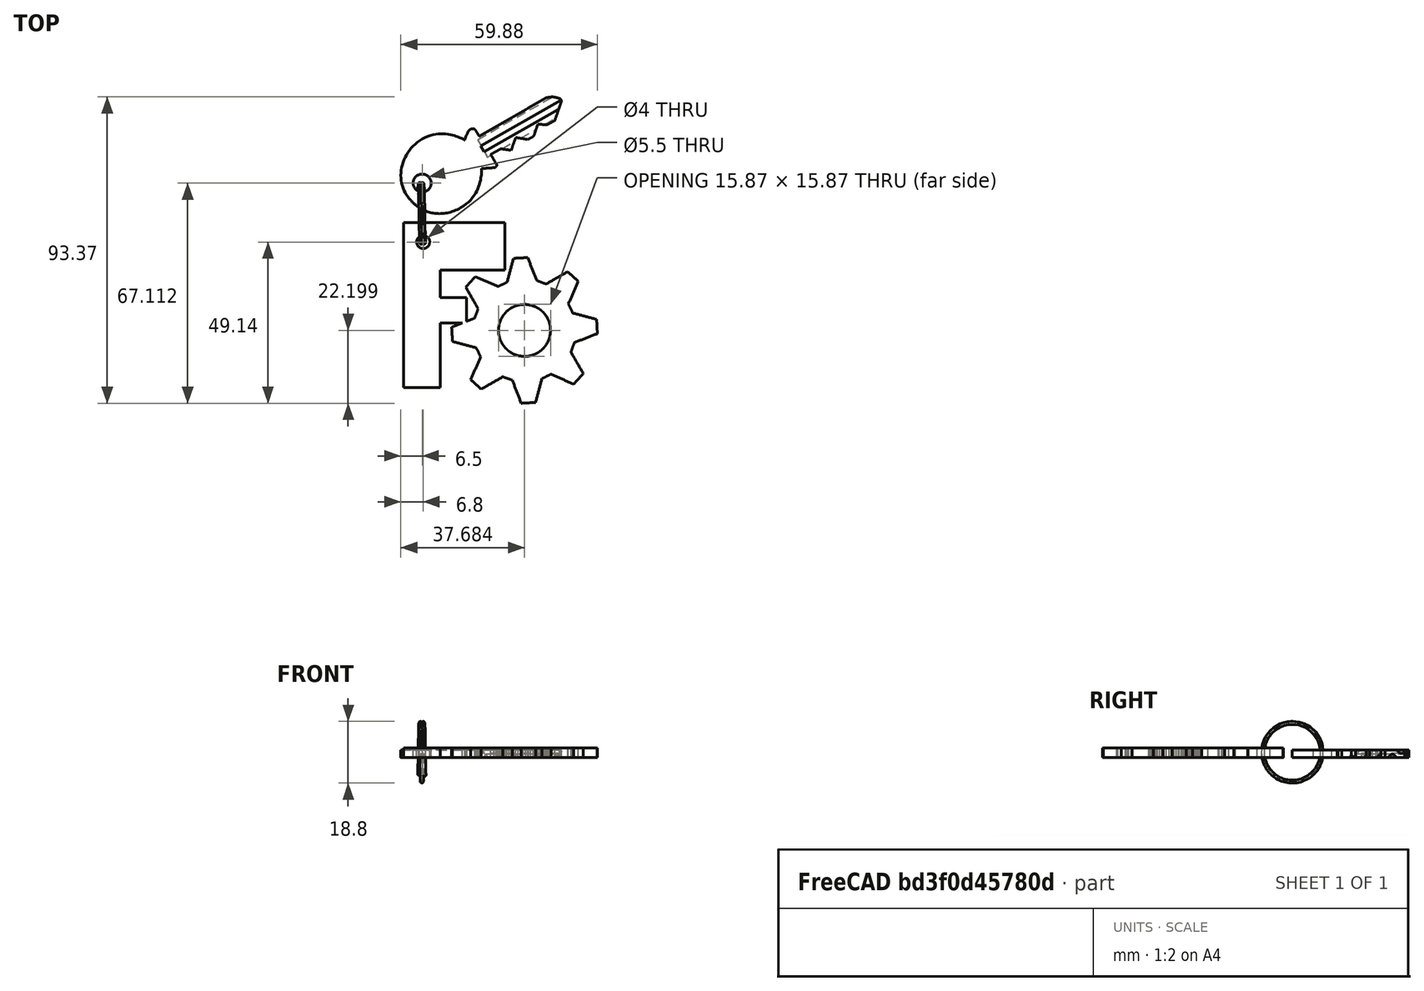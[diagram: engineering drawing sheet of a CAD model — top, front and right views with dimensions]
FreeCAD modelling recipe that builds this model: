
FCSTD DOCUMENT  (FreeCAD 0.15R4630 (Git))
Label: freecad
License: CreativeCommons Attribution-ShareAlike
LicenseURL: http://creativecommons.org/licenses/by-sa/4.0/
objects: Part::Feature×5, Part::Extrusion×3, App::DocumentObjectGroup×2, Part::Cut×2, Part::MultiFuse×1, Part::Cylinder×1
note: 12 computed .brp shape members not serialized (recipe doc carries the construction recipe); baked Part::Feature solids carry a one-line shape summary decoded from their .brp

FEATURE [Part::Feature] Sweep  label="key-ring-model-1"
  Placement = pos=(-1.2,24.7546,1.6391) rot=(0.333333,0.881918,0.333333;1.69612rad)
  shape: bbox 3.31 x 27.02 x 26.33 mm, 4 faces (baked)
FEATURE [Part::Feature] Cut  label="key-model-1"
  Placement = pos=(-5.46976,31.0266,0) rot=(0,0,1;0.517888rad)
  shape: bbox 49.82 x 36.6 x 2.3 mm, 44 faces (baked)
FEATURE [App::DocumentObjectGroup] Group  label="Assembly"
  Group = -> [Sweep,Cut]
FEATURE [Part::Feature] rect3663
  shape: bbox 30.8 x 50.38 x 7.562e-07 mm, 0 faces, 0 solids (baked)
FEATURE [Part::Feature] path3659
  shape: bbox 44.4 x 44.4 x 7.562e-07 mm, 0 faces, 0 solids (baked)
FEATURE [Part::Feature] path3659001
  shape: bbox 15.87 x 15.87 x 7.562e-07 mm, 0 faces, 0 solids (baked)
FEATURE [Part::Extrusion] Extrude
  Base = -> rect3663
  Dir = (0,0,3)
  Solid = true
FEATURE [Part::Extrusion] Extrude001
  Base = -> path3659
  Dir = (0,0,3)
  Solid = true
FEATURE [Part::Extrusion] Extrude002
  Base = -> path3659001
  Dir = (0,0,3)
  Solid = true
FEATURE [Part::Cut] Cut001
  Base = -> Extrude001
  Tool = -> Extrude002
FEATURE [Part::MultiFuse] Fusion  label="Logo"
  Shapes = -> [Extrude,Cut001]
FEATURE [Part::Cylinder] Cylinder  label="drill"
  Angle = 360
  Height = 10
  Placement = pos=(7,-7,0) rot=(0,0,1;0rad)
  Radius = 2
FEATURE [Part::Cut] Cut002  label="freecad-key"
  Base = -> Fusion
  Placement = pos=(-7,23,0) rot=(0,0,1;0rad)
  Tool = -> Cylinder
FEATURE [App::DocumentObjectGroup] Grupo  label="FreeCAD_logo"
  Group = -> [Cut002]
